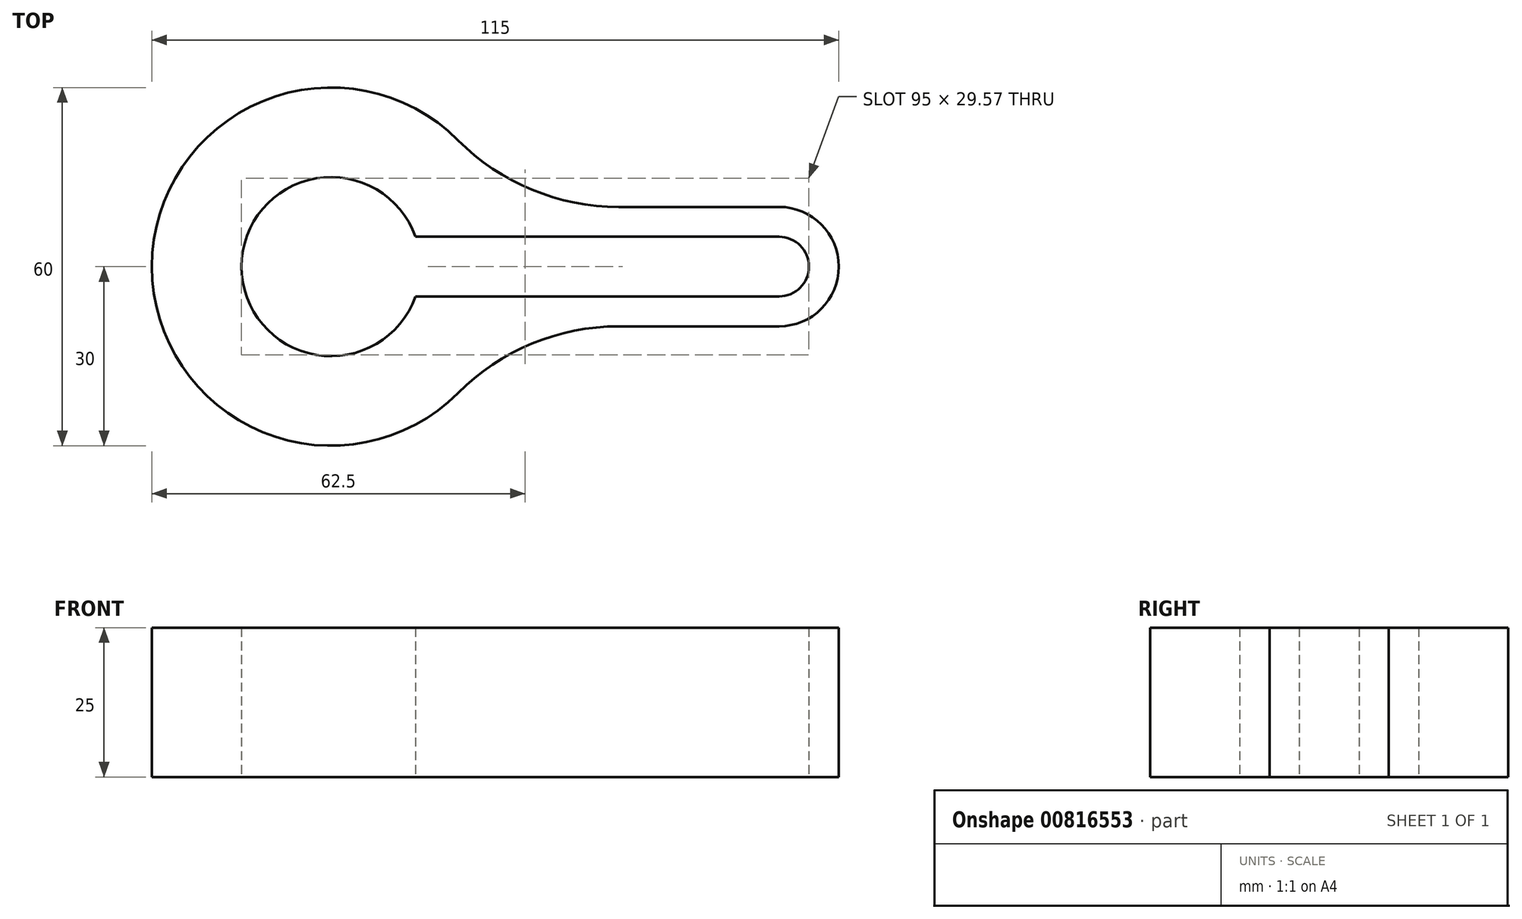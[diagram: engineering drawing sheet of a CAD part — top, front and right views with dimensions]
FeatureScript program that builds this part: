
annotation { "Feature Type Name" : "Feature", "Feature Type Description" : "" }
export const myFeature = defineFeature(function(context is Context, id is Id, definition is map)
    precondition{}
    {
        {
            var Q0;
            Q0=qCreatedBy(makeId("Top.planeOp"),FACE);
            var sketch = newSketch(context, id + "F0", { "sketchPlane" : qUnion([Q0])});
            skArc(sketch, "E0", {"start": v(14.14, 5) * mm, "mid": v(-15, 0) * mm, "end": v(14.14, -5) * mm});
            skArc(sketch, "E1", {"start": v(75, -5) * mm, "mid": v(80, 0) * mm, "end": v(75, 5) * mm});
            skLineSegment(sketch, "E2.top", {"start": v(14.14, 5) * mm, "end": v(75, 5) * mm});
            skLineSegment(sketch, "E3.top", {"start": v(14.14, -5) * mm, "end": v(75, -5) * mm});
            skPoint(sketch, "E2.right.end.orphan", {"position": v(75, 5) * mm});
            skPoint(sketch, "E3.right.end.orphan", {"position": v(75, -5) * mm});
            skPoint(sketch, "E3.left.end.orphan", {"position": v(0, -5) * mm});
            skArc(sketch, "E4.0", {"start": v(21.25, 21.18) * mm, "mid": v(-30, 0) * mm, "end": v(21.25, -21.18) * mm});
            skLineSegment(sketch, "E5.0", {"start": v(48.17, 10) * mm, "end": v(75, 10) * mm});
            skLineSegment(sketch, "E6.0", {"start": v(48.17, -10) * mm, "end": v(75, -10) * mm});
            skArc(sketch, "E7.0", {"start": v(75, -10) * mm, "mid": v(85, 0) * mm, "end": v(75, 10) * mm});
            skArc(sketch, "E8", {"start": v(21.25, 21.18) * mm, "mid": v(33.6, 12.9) * mm, "end": v(48.17, 10) * mm});
            skArc(sketch, "E9", {"start": v(48.17, -10) * mm, "mid": v(33.6, -12.9) * mm, "end": v(21.25, -21.18) * mm});
            skSolve(sketch);
        }
        {
            var Q0;
            Q0=makeQuery(id+"F0.imprint","IMPRINT",FACE,{"disambiguationData":[TD([[makeQuery(id+"F0.imprint","IMPRINT",EDGE,{"derivedFrom":sQuery(id+"F0.wireOp",EDGE,"E0")}),-1.0]])]});
            extrude(context, id + "F1", {"entities" : qUnion([Q0]), "depth" : 25 * mm, "offsetDistance" : 25 * mm});
        }
    });
